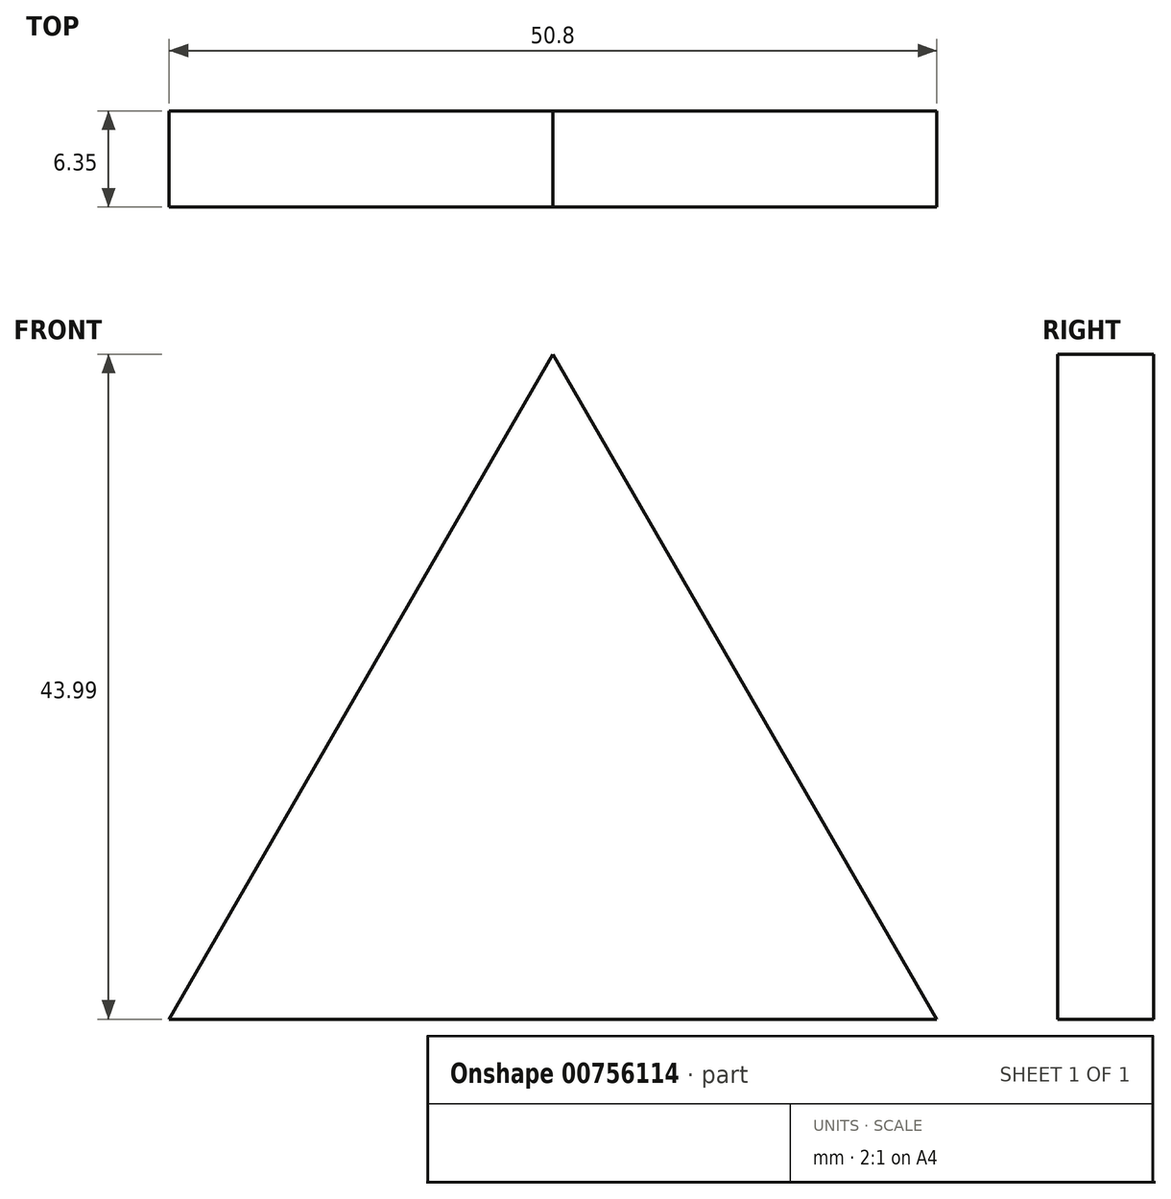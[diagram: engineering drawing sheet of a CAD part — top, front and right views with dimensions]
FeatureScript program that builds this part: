
annotation { "Feature Type Name" : "Feature", "Feature Type Description" : "" }
export const myFeature = defineFeature(function(context is Context, id is Id, definition is map)
    precondition{}
    {
        {
            var Q0;
            Q0=qCreatedBy(makeId("Front.planeOp"),FACE);
            var sketch = newSketch(context, id + "F0", { "sketchPlane" : qUnion([Q0])});
            skLineSegment(sketch, "E0", {"start": v(-106.34, 44) * mm, "end": v(-131.74, 0) * mm});
            skLineSegment(sketch, "E1", {"start": v(-131.74, 0) * mm, "end": v(-80.94, 0) * mm});
            skLineSegment(sketch, "E2", {"start": v(-80.94, 0) * mm, "end": v(-106.34, 44) * mm});
            skSolve(sketch);
        }
        {
            var Q0;
            Q0=makeQuery(id+"F0.imprint","IMPRINT",FACE,{"disambiguationData":[TD([[makeQuery(id+"F0.imprint","IMPRINT",EDGE,{"derivedFrom":sQuery(id+"F0.wireOp",EDGE,"E0")}),1.0]])]});
            extrude(context, id + "F1", {"entities" : qUnion([Q0]), "depth" : 6.35 * mm, "offsetDistance" : 25.4 * mm});
        }
    });
